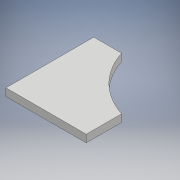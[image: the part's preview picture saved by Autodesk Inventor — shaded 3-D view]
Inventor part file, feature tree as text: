
AUTODESK INVENTOR PART (.ipt)
format: ipt  version: 2018 (Build 220112000, 112)  size: 104,960 bytes
history: native  units: mm
features: other x1, extrude x1
ambient origin geometry x8: Origin, YZ Plane, XZ Plane, XY Plane, X Axis, Y Axis, Z Axis, Center Point
bodies: Body1 (feature_tree)
feature tree (2):
  other  "Bryła1"
  extrude  "Wyciągnięcie proste1"  Depth=6.0mm TaperAngle=0.0deg
